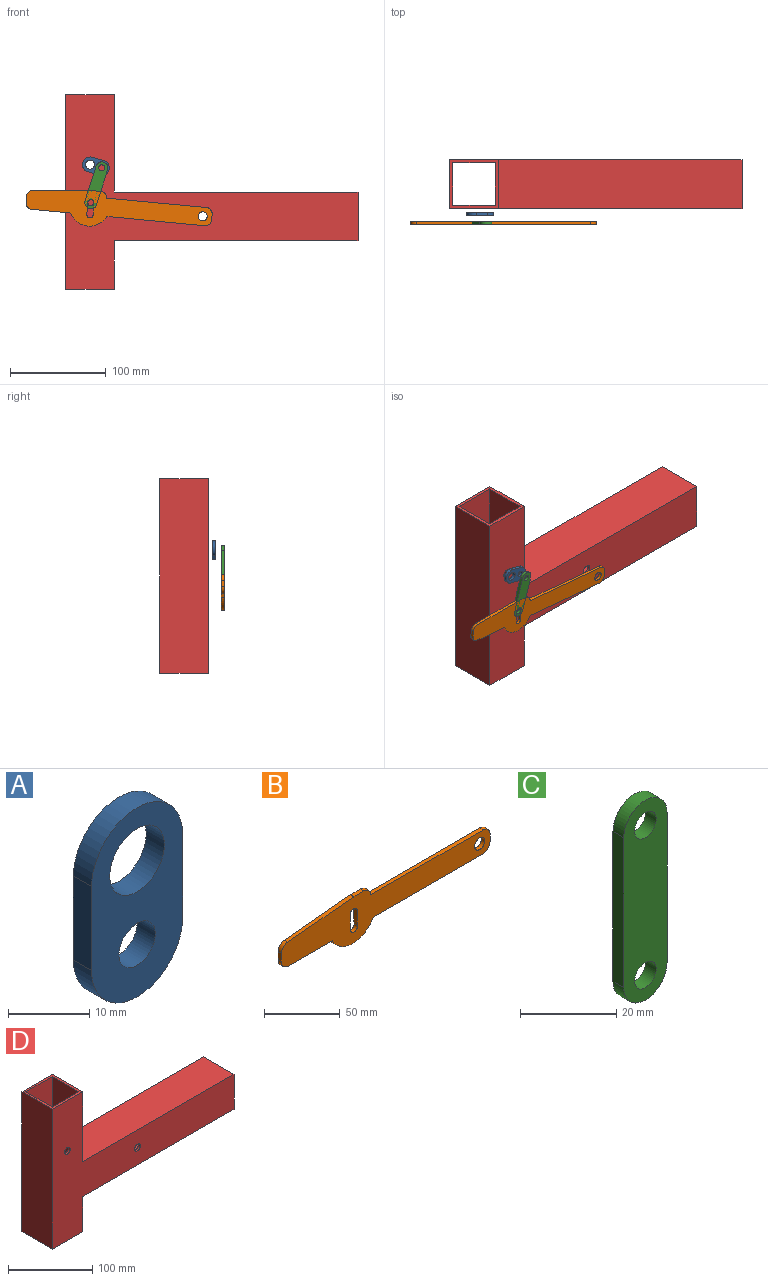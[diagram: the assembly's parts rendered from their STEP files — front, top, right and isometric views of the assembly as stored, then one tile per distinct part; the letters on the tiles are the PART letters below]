
ASSEMBLY  parts=4 mates=3
PART A: 8 faces, bbox 15.9x3.2x28.6 mm
  f0: cylinder r=7.94mm len=15.88mm, axis (0,1,0), area 79.2mm2, adj f1,f3,f6,f7
  f1: plane 12.7x3.18mm, normal (1,0,0), area 40.3mm2, adj f0,f2,f6,f7
  f2: cylinder r=7.94mm len=15.88mm, axis (0,1,0), area 79.2mm2, adj f1,f3,f6,f7
  f3: plane 12.7x3.18mm, normal (-1,0,0), area 40.3mm2, adj f0,f2,f6,f7
  f4: cylinder r=3.17mm len=6.35mm, axis (0,1,0), area 63.3mm2, adj f6,f7
  f5: cylinder r=4.76mm len=9.53mm, axis (0,1,0), area 95mm2, adj f6,f7
  f6: plane 28.58x15.88mm, normal (0,-1,0), area 296.6mm2, adj f0,f1,f2,f3,f4,f5
  f7: plane 28.58x15.88mm, normal (0,1,0), area 296.6mm2, adj f0,f1,f2,f3,f4,f5
PART B: 21 faces, bbox 194.3x3.2x37.3 mm
  f0: plane 194.31x37.28mm, normal (0,-1,0), area 4111.3mm2, adj f2,f3,f4,f5,f6,f7,f8,f9
  f1: plane 194.31x37.28mm, normal (0,1,0), area 4111.3mm2, adj f2,f3,f4,f5,f6,f7,f8,f9
  f2: plane 102.56x3.18mm, normal (0,0,-1), area 325.6mm2, adj f0,f1,f12,f17
  f3: plane 61.26x5.78mm, normal (-0.09,0,1), area 195.4mm2, adj f0,f1,f10,f15
  f4: plane 6.92x3.18mm, normal (-1,0,0), area 22mm2, adj f0,f1,f10,f11
  f5: plane 41.06x3.18mm, normal (0,0,-1), area 130.4mm2, adj f0,f1,f11,f17
  f6: plane 6.35x3.18mm, normal (1,0,0), area 20.2mm2, adj f0,f1,f12,f13
  f7: plane 104.78x3.18mm, normal (0,0,1), area 332.7mm2, adj f0,f1,f13,f14
  f8: plane 9.23x3.18mm, normal (0,0,1), area 29.3mm2, adj f0,f1,f14,f15
  f9: cylinder r=4.76mm len=9.53mm, axis (0,1,0), area 95mm2, adj f0,f1
  f10: cylinder r=6.35mm len=6.32mm, axis (0,-1,0), area 29.8mm2, adj f0,f1,f3,f4
  f11: cylinder r=6.35mm len=6.35mm, axis (0,1,0), area 31.7mm2, adj f0,f1,f4,f5
  f12: cylinder r=6.35mm len=6.35mm, axis (0,-1,0), area 31.7mm2, adj f0,f1,f2,f6
  f13: cylinder r=6.35mm len=6.35mm, axis (0,-1,0), area 31.7mm2, adj f0,f1,f6,f7
  f14: cylinder r=6.35mm len=6.35mm, axis (0,1,0), area 31.7mm2, adj f0,f1,f7,f8
  f15: cylinder r=6.35mm len=3.18mm, axis (0,1,0), area 1.9mm2, adj f0,f1,f3,f8
  f16: cylinder r=120.76mm len=13.05mm, axis (0,-1,0), area 41.5mm2, adj f0,f1,f18,f20
  f17: cylinder r=21.13mm len=38mm, axis (0,-1,0), area 150mm2, adj f0,f1,f2,f5
  f18: cylinder r=3.24mm len=6.47mm, axis (0,-1,0), area 32.3mm2, adj f0,f1,f16,f19
  f19: cylinder r=114.28mm len=12.35mm, axis (0,-1,0), area 39.2mm2, adj f0,f1,f18,f20
  f20: cylinder r=3.24mm len=6.48mm, axis (0,-1,0), area 32.3mm2, adj f0,f1,f16,f19
PART C: 8 faces, bbox 12.7x3.2x50.8 mm
  f0: plane 38.1x3.18mm, normal (-1,0,0), area 121mm2, adj f1,f4,f6,f7
  f1: cylinder r=6.35mm len=12.7mm, axis (0,1,0), area 63.3mm2, adj f0,f2,f6,f7
  f2: plane 38.1x3.18mm, normal (1,0,0), area 121mm2, adj f1,f4,f6,f7
  f3: cylinder r=3.17mm len=6.35mm, axis (0,1,0), area 63.3mm2, adj f6,f7
  f4: cylinder r=6.35mm len=12.7mm, axis (0,1,0), area 63.3mm2, adj f0,f2,f6,f7
  f5: cylinder r=3.17mm len=6.35mm, axis (0,1,0), area 63.3mm2, adj f6,f7
  f6: plane 50.8x12.7mm, normal (0,-1,0), area 547.2mm2, adj f0,f1,f2,f3,f4,f5
  f7: plane 50.8x12.7mm, normal (0,1,0), area 547.2mm2, adj f0,f1,f2,f3,f4,f5
PART D: 23 faces, bbox 304.8x50.8x203.2 mm
  f0: plane 101.6x50.8mm, normal (1,0,0), area 5161.3mm2, adj f2,f8,f9,f11
  f1: plane 203.2x50.8mm, normal (-1,0,0), area 10322.6mm2, adj f2,f8,f9,f10
  f2: plane 304.8x203.2mm, normal (0,-1,0), area 23083.2mm2, adj f0,f1,f3,f9,f10,f11,f12,f17
  f3: plane 50.8x50.8mm, normal (1,0,0), area 2580.6mm2, adj f2,f8,f10,f12
  f4: plane 203.2x44.45mm, normal (0,1,0), area 8961mm2, adj f5,f7,f9,f10,f22
  f5: plane 203.2x44.45mm, normal (1,0,0), area 9032.2mm2, adj f4,f6,f9,f10
  f6: plane 203.2x44.45mm, normal (0,-1,0), area 8961mm2, adj f5,f7,f9,f10,f21
  f7: plane 203.2x44.45mm, normal (-1,0,0), area 9032.2mm2, adj f4,f6,f9,f10
  f8: plane 304.8x203.2mm, normal (0,1,0), area 23083.2mm2, adj f0,f1,f3,f9,f10,f11,f12,f17
  f9: plane 50.8x50.8mm, normal (0,0,1), area 604.8mm2, adj f0,f1,f2,f4,f5,f6,f7,f8
  f10: plane 50.8x50.8mm, normal (0,0,-1), area 604.8mm2, adj f1,f2,f3,f4,f5,f6,f7,f8
  f11: plane 254x50.8mm, normal (0,0,1), area 12903.2mm2, adj f0,f2,f8,f17
  f12: plane 254x50.8mm, normal (0,0,-1), area 12903.2mm2, adj f2,f3,f8,f17
  f13: plane 254x44.45mm, normal (0,-1,0), area 11219mm2, adj f14,f16,f17,f18,f20
  f14: plane 254x44.45mm, normal (0,0,1), area 11290.3mm2, adj f13,f15,f17,f18
  f15: plane 254x44.45mm, normal (0,1,0), area 11219mm2, adj f14,f16,f17,f18,f19
  f16: plane 254x44.45mm, normal (0,0,-1), area 11290.3mm2, adj f13,f15,f17,f18
  f17: plane 50.8x50.8mm, normal (1,0,0), area 604.8mm2, adj f2,f8,f11,f12,f13,f14,f15,f16
  f18: plane 44.45x44.45mm, normal (1,0,0), area 1975.8mm2, adj f13,f14,f15,f16
  f19: cylinder r=4.76mm len=9.53mm, axis (0,-1,0), area 95mm2, adj f2,f15
  f20: cylinder r=4.76mm len=9.53mm, axis (0,-1,0), area 95mm2, adj f8,f13
  f21: cylinder r=4.76mm len=9.53mm, axis (0,-1,0), area 95mm2, adj f6,f8
  f22: cylinder r=4.76mm len=9.53mm, axis (0,-1,0), area 95mm2, adj f2,f4
PLACE A rot(axis=(0,-1,0),74.5deg) t=(27.53,118.95,-72.21)mm
PLACE B rot(axis=(0,1,0),5.4deg) t=(-86.02,109.39,-68.16)mm
PLACE C rot(axis=(0,1,0),17.4deg) t=(-89.89,112.57,-57.07)mm
PLACE D t=(-84.36,122.76,-83.91)mm fixed
MATE cylindrical A.f2 <-> D.f21  axis (0,1,0) through (-36.1,66.56,-4.53)mm
MATE cylindrical D.f19 <-> B.f9  axis (0,-1,0) through (81.37,121.17,-58.51)mm
MATE cylindrical A.f0 <-> C.f3  axis (0,1,0) through (-23.86,66.56,-7.92)mm
